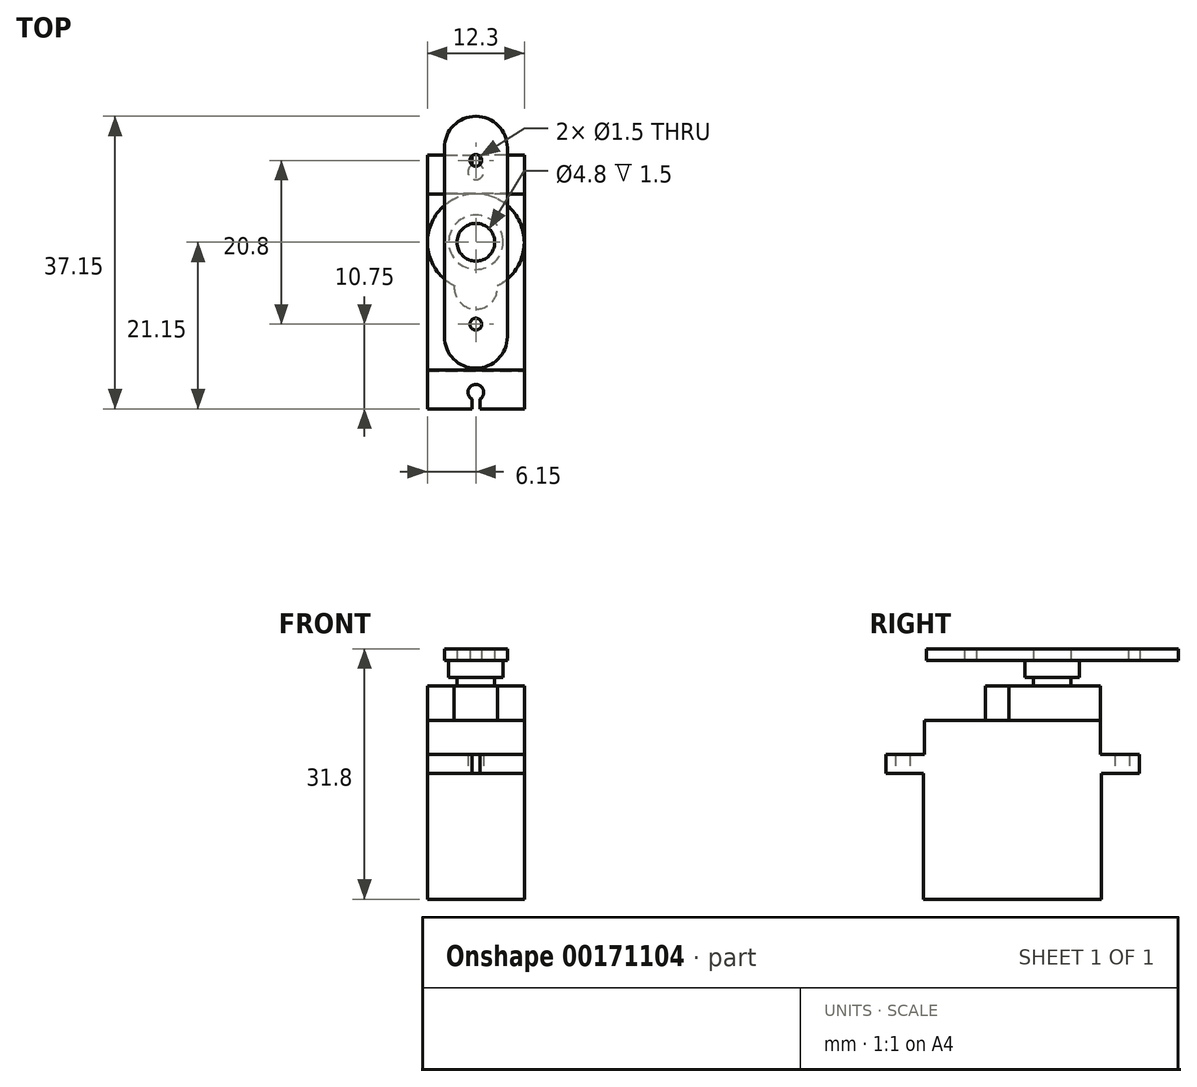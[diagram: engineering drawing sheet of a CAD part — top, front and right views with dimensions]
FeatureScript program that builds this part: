
annotation { "Feature Type Name" : "Feature", "Feature Type Description" : "" }
export const myFeature = defineFeature(function(context is Context, id is Id, definition is map)
    precondition{}
    {
        {
            var Q0;
            Q0=qCreatedBy(makeId("Top.planeOp"),FACE);
            var sketch = newSketch(context, id + "F0", { "sketchPlane" : qUnion([Q0])});
            skLineSegment(sketch, "E0.bottom", {"start": v(6.15, -16.1) * mm, "end": v(-6.15, -16.1) * mm, "construction": true});
            skLineSegment(sketch, "E0.top", {"start": v(6.15, 16.1) * mm, "end": v(-6.15, 16.1) * mm, "construction": true});
            skLineSegment(sketch, "E0.left", {"start": v(6.15, -16.1) * mm, "end": v(6.15, 16.1) * mm});
            skLineSegment(sketch, "E0.right", {"start": v(-6.15, -16.1) * mm, "end": v(-6.15, 16.1) * mm});
            skPoint(sketch, "E0.middle", {"position": v(0, 0) * mm});
            skArc(sketch, "E1", {"start": v(0.5, 14.87) * mm, "mid": v(0, 13) * mm, "end": v(-0.5, 14.87) * mm});
            skArc(sketch, "E2", {"start": v(-0.5, -14.87) * mm, "mid": v(0, -13) * mm, "end": v(0.5, -14.87) * mm});
            skLineSegment(sketch, "E3", {"start": v(-0.5, -14.87) * mm, "end": v(-0.5, -16.1) * mm});
            skLineSegment(sketch, "E4", {"start": v(-0.5, -16.1) * mm, "end": v(-6.15, -16.1) * mm});
            skLineSegment(sketch, "E5", {"start": v(0.5, -14.87) * mm, "end": v(0.5, -16.1) * mm});
            skLineSegment(sketch, "E6", {"start": v(0.5, -16.1) * mm, "end": v(6.15, -16.1) * mm});
            skLineSegment(sketch, "E7", {"start": v(-6.15, 16.1) * mm, "end": v(-0.5, 16.1) * mm});
            skLineSegment(sketch, "E8", {"start": v(-0.5, 16.1) * mm, "end": v(-0.5, 14.87) * mm});
            skLineSegment(sketch, "E9", {"start": v(6.15, 16.1) * mm, "end": v(0.5, 16.1) * mm});
            skLineSegment(sketch, "E10", {"start": v(0.5, 16.1) * mm, "end": v(0.5, 14.87) * mm});
            skSolve(sketch);
        }
        {
            var Q0;
            Q0=makeQuery(id+"F0.imprint","IMPRINT",FACE,{"disambiguationData":[TD([[makeQuery(id+"F0.imprint","IMPRINT",EDGE,{"derivedFrom":sQuery(id+"F0.wireOp",EDGE,"E0.left")}),1.0]])]});
            extrude(context, id + "F1", {"entities" : qUnion([Q0]), "depth" : 2.4 * mm});
        }
        {
            var Q0;
            Q0=makeQuery(id+"F1.opExtrude","CAP_FACE",FACE,{"disambiguationData":[OSD([sQuery(id+"F0.wireOp",EDGE,"E0.left"),sQuery(id+"F0.wireOp",EDGE,"E0.right"),sQuery(id+"F0.wireOp",EDGE,"E1"),sQuery(id+"F0.wireOp",EDGE,"E2"),sQuery(id+"F0.wireOp",EDGE,"E3"),sQuery(id+"F0.wireOp",EDGE,"E4"),sQuery(id+"F0.wireOp",EDGE,"E5"),sQuery(id+"F0.wireOp",EDGE,"E6"),sQuery(id+"F0.wireOp",EDGE,"E7"),sQuery(id+"F0.wireOp",EDGE,"E8"),sQuery(id+"F0.wireOp",EDGE,"E9"),sQuery(id+"F0.wireOp",EDGE,"E10")])],"isStart":false});
            var sketch = newSketch(context, id + "F2", { "sketchPlane" : qUnion([Q0])});
            skLineSegment(sketch, "E11.bottom", {"start": v(6.15, 11.2) * mm, "end": v(-6.15, 11.2) * mm});
            skLineSegment(sketch, "E11.top", {"start": v(6.15, -11.2) * mm, "end": v(-6.15, -11.2) * mm});
            skLineSegment(sketch, "E11.left", {"start": v(6.15, 11.2) * mm, "end": v(6.15, -11.2) * mm});
            skLineSegment(sketch, "E11.right", {"start": v(-6.15, 11.2) * mm, "end": v(-6.15, -11.2) * mm});
            skPoint(sketch, "E11.middle", {"position": v(0, 0) * mm});
            skSolve(sketch);
        }
        {
            var Q0;
            Q0 = qSketchRegion(id + "F2", true);
            extrude(context, id + "F3", {"entities" : qUnion([Q0]), "operationType" : NewBodyOperationType.ADD, "depth" : 4.3 * mm});
        }
        {
            var Q0;
            Q0=makeQuery(id+"F3.opExtrude","CAP_FACE",FACE,{"disambiguationData":[OSD([sQuery(id+"F2.wireOp",EDGE,"E11.bottom"),sQuery(id+"F2.wireOp",EDGE,"E11.top"),sQuery(id+"F2.wireOp",EDGE,"E11.left"),sQuery(id+"F2.wireOp",EDGE,"E11.right")])],"isStart":false});
            var sketch = newSketch(context, id + "F4", { "sketchPlane" : qUnion([Q0])});
            skArc(sketch, "E12", {"start": v(-2.74, -0.46) * mm, "mid": v(0, 11.2) * mm, "end": v(2.74, -0.46) * mm});
            skArc(sketch, "E13", {"start": v(-2.74, -0.46) * mm, "mid": v(0, -3.45) * mm, "end": v(2.74, -0.46) * mm});
            skLineSegment(sketch, "E14", {"start": v(-3.48, -3.45) * mm, "end": v(2.82, -3.45) * mm, "construction": true});
            skSolve(sketch);
        }
        {
            var Q0;
            {var subQ0=sQuery(id+"F4.wireOp",EDGE,"E13");Q0=makeQuery(id+"F4.imprint","IMPRINT",FACE,{"disambiguationData":[TD([[makeQuery(id+"F4.imprint","IMPRINT",EDGE,{"derivedFrom":subQ0}),1.0]])]});}
            extrude(context, id + "F5", {"entities" : qUnion([Q0]), "operationType" : NewBodyOperationType.ADD, "depth" : 4.4 * mm});
        }
        {
            var Q0;
            Q0=makeQuery(id+"F1.opExtrude","CAP_FACE",FACE,{"disambiguationData":[OSD([sQuery(id+"F0.wireOp",EDGE,"E0.left"),sQuery(id+"F0.wireOp",EDGE,"E0.right"),sQuery(id+"F0.wireOp",EDGE,"E1"),sQuery(id+"F0.wireOp",EDGE,"E2"),sQuery(id+"F0.wireOp",EDGE,"E3"),sQuery(id+"F0.wireOp",EDGE,"E4"),sQuery(id+"F0.wireOp",EDGE,"E5"),sQuery(id+"F0.wireOp",EDGE,"E6"),sQuery(id+"F0.wireOp",EDGE,"E7"),sQuery(id+"F0.wireOp",EDGE,"E8"),sQuery(id+"F0.wireOp",EDGE,"E9"),sQuery(id+"F0.wireOp",EDGE,"E10")])],"isStart":true});
            var sketch = newSketch(context, id + "F6", { "sketchPlane" : qUnion([Q0])});
            skLineSegment(sketch, "E15.bottom", {"start": v(-6.15, 11.3) * mm, "end": v(6.15, 11.3) * mm});
            skLineSegment(sketch, "E15.top", {"start": v(-6.15, -11.3) * mm, "end": v(6.15, -11.3) * mm});
            skLineSegment(sketch, "E15.left", {"start": v(-6.15, 11.3) * mm, "end": v(-6.15, -11.3) * mm});
            skLineSegment(sketch, "E15.right", {"start": v(6.15, 11.3) * mm, "end": v(6.15, -11.3) * mm});
            skPoint(sketch, "E15.middle", {"position": v(0, 0) * mm});
            skSolve(sketch);
        }
        {
            var Q0;
            Q0=makeQuery(id+"F6.imprint","IMPRINT",FACE,{"disambiguationData":[TD([[makeQuery(id+"F6.imprint","IMPRINT",EDGE,{"derivedFrom":sQuery(id+"F6.wireOp",EDGE,"E15.bottom")}),-1.0]])]});
            extrude(context, id + "F7", {"entities" : qUnion([Q0]), "operationType" : NewBodyOperationType.ADD, "depth" : 16 * mm});
        }
        {
            var Q0;
            Q0=makeQuery(id+"F5.opExtrude","CAP_FACE",FACE,{"disambiguationData":[OSD([sQuery(id+"F4.wireOp",EDGE,"E12"),sQuery(id+"F4.wireOp",EDGE,"E13")])],"isStart":false});
            var sketch = newSketch(context, id + "F8", { "sketchPlane" : qUnion([Q0])});
            skCircle(sketch, "E16", {"center": v(0, 5.05) * mm, "radius": 2.4 * mm});
            skSolve(sketch);
        }
        {
            var Q0;
            Q0 = qSketchRegion(id + "F8", true);
            extrude(context, id + "F9", {"entities" : qUnion([Q0]), "depth" : 3.2 * mm});
        }
        {
            var Q0;
            Q0=makeQuery(id+"F9.opExtrude","CAP_FACE",FACE,{"disambiguationData":[OSD([sQuery(id+"F8.wireOp",EDGE,"E16")])],"isStart":false});
            var sketch = newSketch(context, id + "F10", { "sketchPlane" : qUnion([Q0])});
            skCircle(sketch, "E17", {"center": v(0, 5.05) * mm, "radius": 2.25 * mm});
            skCircle(sketch, "E18", {"center": v(0, 15.45) * mm, "radius": 0.75 * mm});
            skCircle(sketch, "E19", {"center": v(0, -5.35) * mm, "radius": 0.75 * mm});
            skLineSegment(sketch, "E20", {"start": v(-15.37, 5.05) * mm, "end": v(14.95, 5.05) * mm, "construction": true});
            skLineSegment(sketch, "E21.bottom", {"start": v(4, 21.05) * mm, "end": v(-4, 21.05) * mm});
            skLineSegment(sketch, "E21.top", {"start": v(4, -10.95) * mm, "end": v(-4, -10.95) * mm});
            skLineSegment(sketch, "E21.left", {"start": v(4, 21.05) * mm, "end": v(4, -10.95) * mm});
            skLineSegment(sketch, "E21.right", {"start": v(-4, 21.05) * mm, "end": v(-4, -10.95) * mm});
            skSolve(sketch);
        }
        {
            var Q0;
            Q0=makeQuery(id+"F10.imprint","IMPRINT",FACE,{"disambiguationData":[TD([[makeQuery(id+"F10.imprint","IMPRINT",EDGE,{"derivedFrom":sQuery(id+"F10.wireOp",EDGE,"E18")}),-1.0]])]});
            extrude(context, id + "F11", {"entities" : qUnion([Q0]), "depth" : 1.5 * mm});
        }
        {
            var Q0;
            Q0=makeQuery(id+"F11.opExtrude","CAP_FACE",FACE,{"disambiguationData":[OSD([sQuery(id+"F8.wireOp",EDGE,"E16"),sQuery(id+"F10.wireOp",EDGE,"E18"),sQuery(id+"F10.wireOp",EDGE,"E19"),sQuery(id+"F10.wireOp",EDGE,"E21.bottom"),sQuery(id+"F10.wireOp",EDGE,"E21.top"),sQuery(id+"F10.wireOp",EDGE,"E21.left"),sQuery(id+"F10.wireOp",EDGE,"E21.right")])],"isStart":true});
            var sketch = newSketch(context, id + "F12", { "sketchPlane" : qUnion([Q0])});
            skCircle(sketch, "E22", {"center": v(0, -5.05) * mm, "radius": 3.45 * mm});
            skSolve(sketch);
        }
        {
            var Q0;
            Q0=makeQuery(id+"F12.imprint","IMPRINT",FACE,{"disambiguationData":[TD([[makeQuery(id+"F12.imprint","IMPRINT",EDGE,{"derivedFrom":sQuery(id+"F12.wireOp",EDGE,"E22")}),1.0]])]});
            extrude(context, id + "F13", {"entities" : qUnion([Q0]), "operationType" : NewBodyOperationType.ADD, "depth" : 2.15 * mm});
        }
        {
            var Q0;
            Q0=makeQuery(id+"F11.opExtrude","SWEPT_EDGE",EDGE,{"disambiguationData":[OSD([sQuery(id+"F10.wireOp",EDGE,"E21.bottom"),sQuery(id+"F10.wireOp",EDGE,"E21.left")])]});
            var Q1;
            Q1=makeQuery(id+"F11.opExtrude","SWEPT_EDGE",EDGE,{"disambiguationData":[OSD([sQuery(id+"F10.wireOp",EDGE,"E21.bottom"),sQuery(id+"F10.wireOp",EDGE,"E21.right")])]});
            var Q2;
            Q2=makeQuery(id+"F11.opExtrude","SWEPT_EDGE",EDGE,{"disambiguationData":[OSD([sQuery(id+"F10.wireOp",EDGE,"E21.top"),sQuery(id+"F10.wireOp",EDGE,"E21.left")])]});
            var Q3;
            Q3=makeQuery(id+"F11.opExtrude","SWEPT_EDGE",EDGE,{"disambiguationData":[OSD([sQuery(id+"F10.wireOp",EDGE,"E21.top"),sQuery(id+"F10.wireOp",EDGE,"E21.right")])]});
            fillet(context, id + "F14", {"entities" : qUnion([Q0, Q1, Q2, Q3]), "radius" : 4 * mm, "tangentPropagation" : true, "allowEdgeOverflow" : false});
        }
    });
